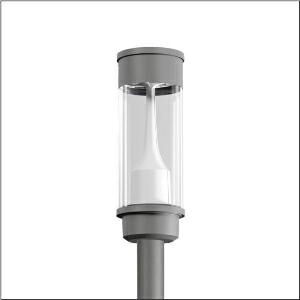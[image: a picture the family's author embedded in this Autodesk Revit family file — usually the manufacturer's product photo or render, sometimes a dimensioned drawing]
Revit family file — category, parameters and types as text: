
# Revit family: litepole_iq___st1_2a_5xa5415ef14h000022_58f2
name_source: partatom
category: Lighting Fixtures
units: mm (PartAtom-declared; Revit-internal decimal feet)

## family parameters
Cut with Voids When Loaded = No
Host = Face
Light Source = No
Part Type = Normal
Room Calculation Point = No
Round Connector Dimension = Use Diameter
Shared = No

## types (1)
- --- (1 x LED, 1540 lm, 10.5 W, 3000K)
    Apparent Load = 11 VA
    CIE Flux Codes = 22 61 93 96 100
    Color Rendering = 70
    Color Temperature = 3000K
    Default Elevation = 1800 mm
    Description = Litepole iQ, mast luminaire, Module 540 iQ-SR, primary light control with 3 zone facetted reflector, of plastic, silver coated, highly specular, structured, primary optical cover: cover, of PMMA, transparent, light distribution: ST1.2a, light emission: direct distribution, primary light characteristic: asymmetric, installation type: post-top, LED, High Power LED, rated luminous flux: 1.540lm, luminous efficacy: 147lm/W, light colour: 730, colour temperature: 3000K, control gear: ECG iQ, control: Street-Remote, Auto-Match, Temp-Guard, Lumen-Switch, Night-Set, Smart-Wire, Light-Fading, Desk-Remote (wireless, voltage-free reading and setting of iQ features in the workshop via application-optimized NFC function/RFID function), optimised constant luminous flux control (CLO 2.0), presetting dimming logarithmic, mains connection: 230..240V, AC, 50/60Hz, connection cable pre-assembled, cable length: 5,5m, wiring characteristics: H07RN-F, start of lifetime: 11W, end of service life: 11W, reduction: 5W, luminaire housing, upper part, of glass-fibre reinforced polyester, coated, Siteco® metallic grey (DB 702S), diameter: 210mm, height: 590mm, spigot size: d x l = 76 x 70mm (post-top) | with reducer (optional accessory) 60 x 70mm, post-top mast mounting element, of diecast aluminium, coated, Siteco® metallic grey (DB 702S), Module 540 iQ-SR, traffic white (RAL 9016), equipment: standard, protection rating (complete): IP65, insulation class (complete): insulation class II (safety insulation), certification: CE, ENEC, VDE, packaging unit: 1 piece

Light Distribution: ST1.2a
    Height = 590 mm
    Lamp = 1 x LED
    Lamp Light Flux = 1540 lm
    Lamp Power = 10.5 W
    Lamp count = 1
    Length = 220 mm
    Luminous efficacy = 147 lm/W
    Manufacturer = Siteco
    ModVariant = No
    Model = 5XA5415EF14H000022
    Number of Poles = 1
    OnlyDefault = Yes
    Power Factor = 1
    Product Name = Litepole iQ | ST1.2a
    Product group = mast luminaire | pylon top
    ProductGroupID = 6100
    Protection Class = Protection class II
    Protection Degree = IP 65
    RLX_Detail_Level = 1
    RLX_Emergency_Light_Flux = 0 lm
    RLX_Emergency_Type = 0
    RLX_Emergency_Type_DB = No
    RlxData = <blob elided: 41169 chars, md5=5b45a83f>
    Socket = socket
    Standby Power = 0 W
    System Light Flux = 1540 lm
    System Power = 11 W
    Type Comments = factory setting: luminous flux: 100 % | dim-lin: 254 | 419 mA
    Type Image = l_1006025.jpg
    URL = http://relux.com
    VarID = @adj_108971
    Voltage = 0 V
    Weight = 0.00 kg
    Width = 0 mm  [stored 0 ft]

note: [stored X ft] marks values corroborated as IEEE doubles in the binary element streams (Revit-internal decimal feet)

## geometry (parser evidence)
native form markers: Blend x4, Sweep x11
no freeform markers — native parametric forms only
